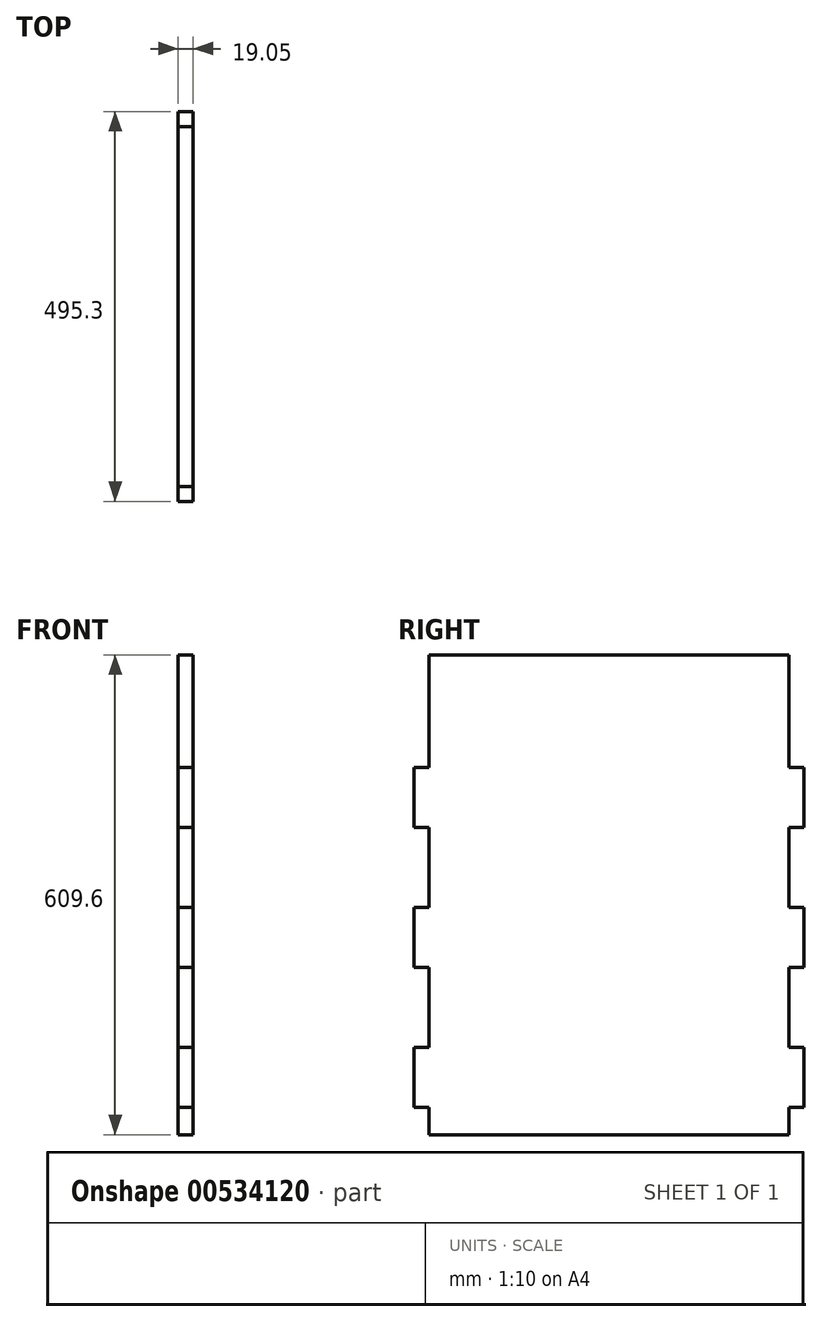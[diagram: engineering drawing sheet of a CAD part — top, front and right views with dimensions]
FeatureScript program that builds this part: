
annotation { "Feature Type Name" : "Feature", "Feature Type Description" : "" }
export const myFeature = defineFeature(function(context is Context, id is Id, definition is map)
    precondition{}
    {
        {
            var Q0;
            Q0=qCreatedBy(makeId("Right.planeOp"),FACE);
            var sketch = newSketch(context, id + "F0", { "sketchPlane" : qUnion([Q0])});
            skLineSegment(sketch, "E0.bottom", {"start": v(0, 0) * mm, "end": v(457.2, 0) * mm});
            skLineSegment(sketch, "E0.top", {"start": v(0, 609.6) * mm, "end": v(457.2, 609.6) * mm});
            skLineSegment(sketch, "E0.left", {"start": v(0, 0) * mm, "end": v(0, 609.6) * mm});
            skLineSegment(sketch, "E0.right", {"start": v(457.2, 0) * mm, "end": v(457.2, 609.6) * mm});
            skLineSegment(sketch, "E1.bottom", {"start": v(457.2, 34.46) * mm, "end": v(476.25, 34.46) * mm});
            skLineSegment(sketch, "E1.top", {"start": v(457.2, 110.66) * mm, "end": v(476.25, 110.66) * mm});
            skLineSegment(sketch, "E1.left", {"start": v(457.2, 34.46) * mm, "end": v(457.2, 110.66) * mm});
            skLineSegment(sketch, "E1.right", {"start": v(476.25, 34.46) * mm, "end": v(476.25, 110.66) * mm});
            skLineSegment(sketch, "E2", {"start": v(457.2, 110.66) * mm, "end": v(457.2, 212.26) * mm, "construction": true});
            skLineSegment(sketch, "E3", {"start": v(457.2, 212.26) * mm, "end": v(457.2, 288.46) * mm});
            skLineSegment(sketch, "E4", {"start": v(457.2, 288.46) * mm, "end": v(457.2, 390.06) * mm, "construction": true});
            skLineSegment(sketch, "E5", {"start": v(457.2, 390.06) * mm, "end": v(457.2, 466.26) * mm});
            skLineSegment(sketch, "E6", {"start": v(457.2, 212.26) * mm, "end": v(476.25, 212.26) * mm});
            skLineSegment(sketch, "E7", {"start": v(457.2, 288.46) * mm, "end": v(476.25, 288.46) * mm});
            skLineSegment(sketch, "E8", {"start": v(457.2, 390.06) * mm, "end": v(476.25, 390.06) * mm});
            skLineSegment(sketch, "E9", {"start": v(457.2, 466.26) * mm, "end": v(476.25, 466.26) * mm});
            skLineSegment(sketch, "E10", {"start": v(476.25, 466.26) * mm, "end": v(476.25, 390.06) * mm});
            skLineSegment(sketch, "E11", {"start": v(476.25, 288.46) * mm, "end": v(476.25, 212.26) * mm});
            skLineSegment(sketch, "E12", {"start": v(228.6, 609.6) * mm, "end": v(228.6, 0) * mm, "construction": true});
            skLineSegment(sketch, "E13.MirrorCS", {"start": v(0, 466.26) * mm, "end": v(-19.05, 466.26) * mm});
            skLineSegment(sketch, "E14.MirrorCS", {"start": v(-19.05, 466.26) * mm, "end": v(-19.05, 390.06) * mm});
            skLineSegment(sketch, "E15.MirrorCS", {"start": v(-19.05, 288.46) * mm, "end": v(-19.05, 212.26) * mm});
            skLineSegment(sketch, "E16.MirrorCS", {"start": v(-19.05, 34.46) * mm, "end": v(-19.05, 110.66) * mm});
            skLineSegment(sketch, "E17.MirrorCS", {"start": v(0, 34.46) * mm, "end": v(-19.05, 34.46) * mm});
            skLineSegment(sketch, "E18.MirrorCS", {"start": v(0, 110.66) * mm, "end": v(-19.05, 110.66) * mm});
            skLineSegment(sketch, "E19.MirrorCS", {"start": v(0, 212.26) * mm, "end": v(-19.05, 212.26) * mm});
            skLineSegment(sketch, "E20.MirrorCS", {"start": v(0, 288.46) * mm, "end": v(-19.05, 288.46) * mm});
            skLineSegment(sketch, "E21.MirrorCS", {"start": v(0, 390.06) * mm, "end": v(-19.05, 390.06) * mm});
            skSolve(sketch);
        }
        {
            var Q0;
            Q0=qSketchRegion(id+"F0",true);
            extrude(context, id + "F1", {"entities" : qUnion([Q0]), "depth" : 19.05 * mm});
        }
    });
